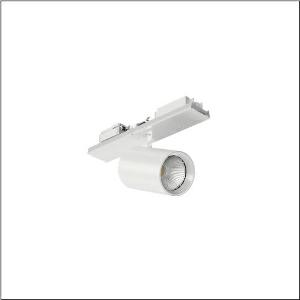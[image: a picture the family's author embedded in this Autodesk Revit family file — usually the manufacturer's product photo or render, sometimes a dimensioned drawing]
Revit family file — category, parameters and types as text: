
# Revit family: licross_spot_31_51sl137a45b
name_source: partatom
category: Lighting Fixtures
units: mm (PartAtom-declared; Revit-internal decimal feet)

## family parameters
Cut with Voids When Loaded = No
Host = Face
Light Source = No
Part Type = Normal
Room Calculation Point = No
Round Connector Dimension = Use Diameter
Shared = No

## types (1)
- --- (1 x LED, 5190 lm, 42.6 W, 4000K)
    Apparent Load = 43 VA
    CIE Flux Codes = 92 97 99 100 100
    Color Rendering = 90
    Color Temperature = 4000K
    Default Elevation = 1800 mm
    Description = Licross Spot 31, directional spotlight, light control with lens, of plastic, LED rated luminous flux: 5.190lm, light colour: 940, with plug, 3-pole, with phase selection, mains connection: 220..240V, AC, 50/60Hz, of aluminium, traffic white (RAL 9016), length: 300mm, diameter: 90mm, protection rating (complete): IP20, insulation class (complete): insulation class I (protective earthing), certification: CE, packaging unit: 1 piece
    Height = 175 mm
    Lamp = 1 x LED
    Lamp Light Flux = 5190 lm
    Lamp Power = 42.6 W
    Lamp count = 1
    Length = 90 mm
    Luminous efficacy = 122 lm/W
    Manufacturer = Siteco
    ModVariant = No
    Model = 51SL137A45B
    Mounting Place = Ceiling
    Mounting Type = Pendant
    Number of Poles = 1
    OnlyDefault = Yes
    Power Factor = 1
    Product Name = Licross Spot 31
    Product group = directional spotlight
    ProductGroupID = 905
    Protection Class = Protection class I
    Protection Degree = IP 20
    RLX_Detail_Level = 1
    RLX_Emergency_Light_Flux = 0 lm
    RLX_Emergency_Type = 0
    RLX_Emergency_Type_DB = No
    RlxData = <blob elided: 14761 chars, md5=c63c802e>
    Socket = socket
    Standby Power = 0 W
    System Light Flux = 5190 lm
    System Power = 43 W
    Type Comments = factory setting: luminous flux: 100 % | (ON | ON | ON) | 1050 mA
    Type Image = l_1245720.jpg
    URL = http://relux.com
    VarID = @adj_133421
    Voltage = 0 V
    Weight = 0.00 kg
    Width = 0 mm  [stored 0 ft]

note: [stored X ft] marks values corroborated as IEEE doubles in the binary element streams (Revit-internal decimal feet)

## geometry (parser evidence)
native form markers: Sweep x9
no freeform markers — native parametric forms only
